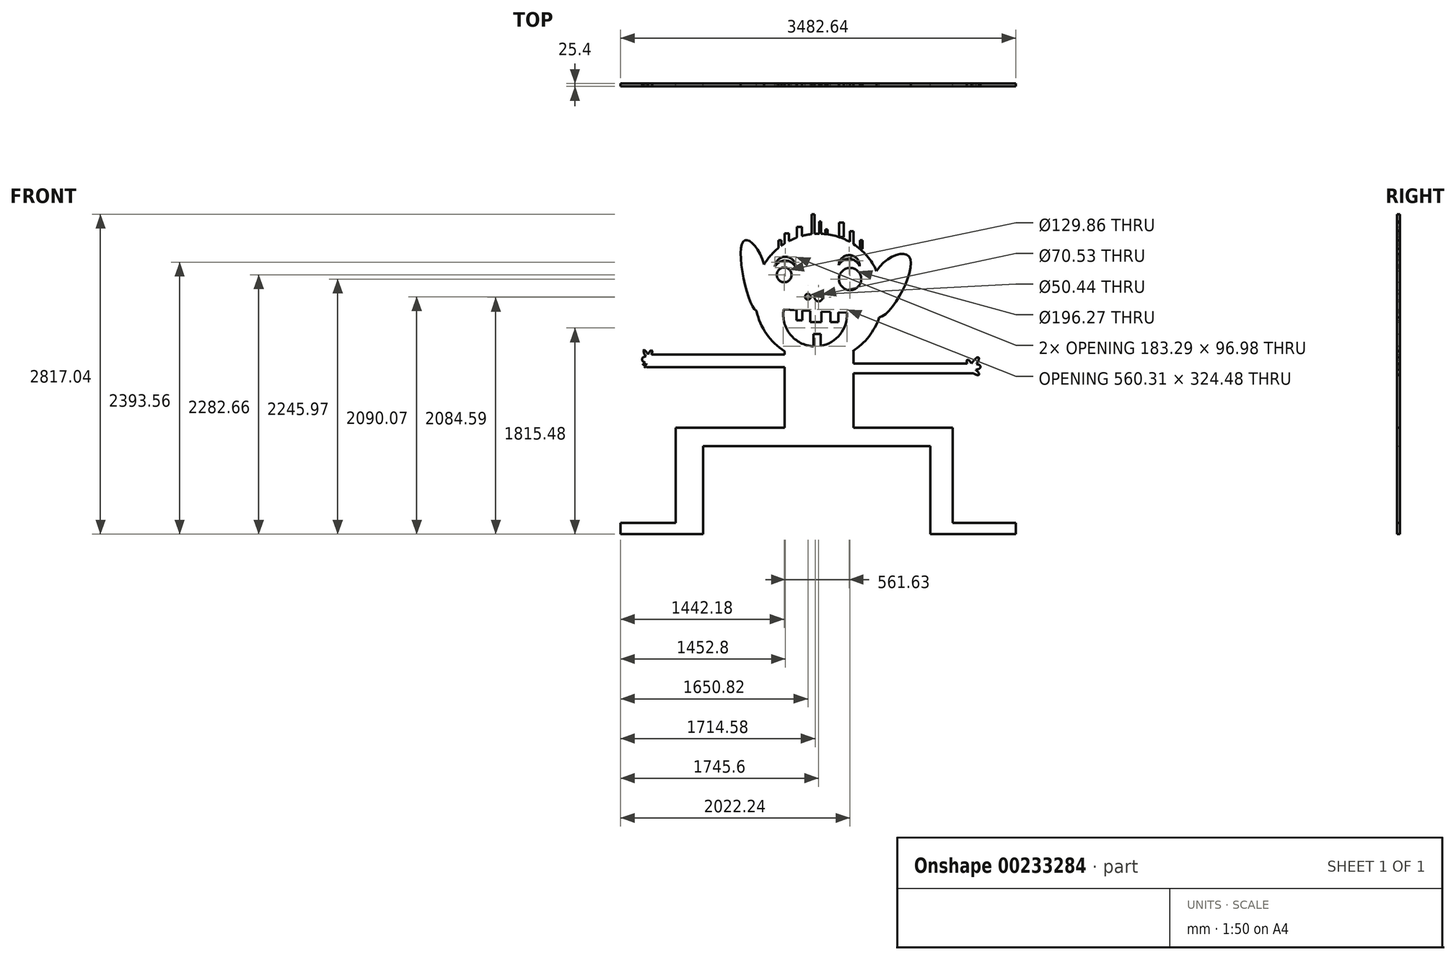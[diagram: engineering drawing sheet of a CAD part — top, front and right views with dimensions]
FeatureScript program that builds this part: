
annotation { "Feature Type Name" : "Feature", "Feature Type Description" : "" }
export const myFeature = defineFeature(function(context is Context, id is Id, definition is map)
    precondition{}
    {
        {
            var Q0;
            Q0=qCreatedBy(makeId("Front.planeOp"),FACE);
            var sketch = newSketch(context, id + "F0", { "sketchPlane" : qUnion([Q0])});
            skCircle(sketch, "E0", {"center": v(-102.15, 2084.59) * mm, "radius": 560.59 * mm});
            skLineSegment(sketch, "E1.bottom", {"start": v(-401.45, 1610.58) * mm, "end": v(205.9, 1610.58) * mm});
            skLineSegment(sketch, "E1.top", {"start": v(-401.45, 775.4) * mm, "end": v(205.9, 775.4) * mm});
            skLineSegment(sketch, "E1.left", {"start": v(-401.45, 1610.58) * mm, "end": v(-401.45, 775.4) * mm});
            skLineSegment(sketch, "E1.right", {"start": v(205.9, 1610.58) * mm, "end": v(205.9, 775.4) * mm});
            skLineSegment(sketch, "E2.bottom", {"start": v(-401.45, 775.4) * mm, "end": v(-1360, 775.4) * mm});
            skLineSegment(sketch, "E2.top", {"start": v(-401.45, 937.97) * mm, "end": v(-1360, 937.97) * mm});
            skLineSegment(sketch, "E2.left", {"start": v(-401.45, 775.4) * mm, "end": v(-401.45, 937.97) * mm});
            skLineSegment(sketch, "E2.right", {"start": v(-1360, 775.4) * mm, "end": v(-1360, 937.97) * mm});
            skLineSegment(sketch, "E3.bottom", {"start": v(-1360, 937.97) * mm, "end": v(-1120.41, 937.97) * mm});
            skLineSegment(sketch, "E3.top", {"start": v(-1360, 0) * mm, "end": v(-1120.41, 0) * mm});
            skLineSegment(sketch, "E3.left", {"start": v(-1360, 937.97) * mm, "end": v(-1360, 0) * mm});
            skLineSegment(sketch, "E3.right", {"start": v(-1120.41, 937.97) * mm, "end": v(-1120.41, 0) * mm});
            skLineSegment(sketch, "E4.bottom", {"start": v(-1120.41, 0) * mm, "end": v(-1847.75, 0) * mm});
            skLineSegment(sketch, "E4.top", {"start": v(-1120.41, 99.4) * mm, "end": v(-1847.75, 99.4) * mm});
            skLineSegment(sketch, "E4.left", {"start": v(-1120.41, 0) * mm, "end": v(-1120.41, 99.4) * mm});
            skLineSegment(sketch, "E4.right", {"start": v(-1847.75, 0) * mm, "end": v(-1847.75, 99.4) * mm});
            skLineSegment(sketch, "E5.bottom", {"start": v(205.9, 775.4) * mm, "end": v(1078.7, 775.4) * mm});
            skLineSegment(sketch, "E5.top", {"start": v(205.9, 937.97) * mm, "end": v(1078.7, 937.97) * mm});
            skLineSegment(sketch, "E5.left", {"start": v(205.9, 775.4) * mm, "end": v(205.9, 937.97) * mm});
            skLineSegment(sketch, "E5.right", {"start": v(1078.7, 775.4) * mm, "end": v(1078.7, 937.97) * mm});
            skLineSegment(sketch, "E6.bottom", {"start": v(1078.7, 937.97) * mm, "end": v(881.89, 937.97) * mm});
            skLineSegment(sketch, "E6.top", {"start": v(1078.7, 0) * mm, "end": v(881.89, 0) * mm});
            skLineSegment(sketch, "E6.left", {"start": v(1078.7, 937.97) * mm, "end": v(1078.7, 0) * mm});
            skLineSegment(sketch, "E6.right", {"start": v(881.89, 937.97) * mm, "end": v(881.89, 0) * mm});
            skLineSegment(sketch, "E7.bottom", {"start": v(881.89, 0) * mm, "end": v(1634.89, 0) * mm});
            skLineSegment(sketch, "E7.top", {"start": v(881.89, 99.4) * mm, "end": v(1634.89, 99.4) * mm});
            skLineSegment(sketch, "E7.left", {"start": v(881.89, 0) * mm, "end": v(881.89, 99.4) * mm});
            skLineSegment(sketch, "E7.right", {"start": v(1634.89, 0) * mm, "end": v(1634.89, 99.4) * mm});
            skLineSegment(sketch, "E8.bottom", {"start": v(205.9, 1417.15) * mm, "end": v(1266.94, 1417.15) * mm});
            skLineSegment(sketch, "E8.top", {"start": v(205.9, 1502.72) * mm, "end": v(1266.94, 1502.72) * mm});
            skLineSegment(sketch, "E8.left", {"start": v(205.9, 1417.15) * mm, "end": v(205.9, 1502.72) * mm});
            skLineSegment(sketch, "E8.right", {"start": v(1266.94, 1417.15) * mm, "end": v(1266.94, 1502.72) * mm});
            skLineSegment(sketch, "E9.bottom", {"start": v(-401.45, 1468.5) * mm, "end": v(-1616.71, 1468.5) * mm});
            skLineSegment(sketch, "E9.top", {"start": v(-401.45, 1579.73) * mm, "end": v(-1616.71, 1579.73) * mm});
            skLineSegment(sketch, "E9.left", {"start": v(-401.45, 1468.5) * mm, "end": v(-401.45, 1579.73) * mm});
            skLineSegment(sketch, "E9.right", {"start": v(-1616.71, 1468.5) * mm, "end": v(-1616.71, 1579.73) * mm});
            skArc(sketch, "E10", {"start": v(-410.16, 1977.72) * mm, "mid": v(-351.42, 1757.13) * mm, "end": v(-148.15, 1653.24) * mm});
            skLineSegment(sketch, "E11", {"start": v(-410.16, 1977.72) * mm, "end": v(-297.9, 1971.72) * mm});
            skCircle(sketch, "E12", {"center": v(-196.93, 2090.07) * mm, "radius": 25.22 * mm});
            skCircle(sketch, "E13", {"center": v(-102.15, 2084.59) * mm, "radius": 35.26 * mm});
            skCircle(sketch, "E14", {"center": v(-405.57, 2282.66) * mm, "radius": 64.93 * mm});
            skCircle(sketch, "E15", {"center": v(174.5, 2245.97) * mm, "radius": 98.13 * mm});
            skLineSegment(sketch, "E16.top", {"start": v(-297.9, 1883.72) * mm, "end": v(-247.37, 1883.72) * mm});
            skLineSegment(sketch, "E16.left", {"start": v(-297.9, 1971.72) * mm, "end": v(-297.9, 1883.72) * mm});
            skLineSegment(sketch, "E16.right", {"start": v(-247.37, 1971.72) * mm, "end": v(-247.37, 1883.72) * mm});
            skLineSegment(sketch, "E17.top", {"start": v(-148.15, 1762.2) * mm, "end": v(-84.59, 1762.2) * mm});
            skLineSegment(sketch, "E17.left", {"start": v(-148.15, 1653.24) * mm, "end": v(-148.15, 1762.2) * mm});
            skLineSegment(sketch, "E17.right", {"start": v(-84.59, 1653.24) * mm, "end": v(-84.59, 1762.2) * mm});
            skLineSegment(sketch, "E18.top", {"start": v(0, 1865.38) * mm, "end": v(71.32, 1865.38) * mm});
            skLineSegment(sketch, "E18.left", {"start": v(0, 1955.78) * mm, "end": v(0, 1865.38) * mm});
            skLineSegment(sketch, "E18.right", {"start": v(71.32, 1955.78) * mm, "end": v(71.32, 1865.38) * mm});
            skLineSegment(sketch, "E19.top", {"start": v(-176.11, 1867.67) * mm, "end": v(-77.71, 1867.67) * mm});
            skLineSegment(sketch, "E19.left", {"start": v(-176.11, 1965.2) * mm, "end": v(-176.11, 1867.67) * mm});
            skLineSegment(sketch, "E19.right", {"start": v(-77.71, 1965.2) * mm, "end": v(-77.71, 1867.67) * mm});
            skLineSegment(sketch, "E20.trimOffspring", {"start": v(-247.37, 1969.01) * mm, "end": v(-176.11, 1965.2) * mm});
            skLineSegment(sketch, "E21.trimOffspring", {"start": v(-77.71, 1959.94) * mm, "end": v(0, 1955.78) * mm});
            skLineSegment(sketch, "E22.trimOffspring", {"start": v(71.32, 1951.96) * mm, "end": v(146.98, 1947.92) * mm});
            skArc(sketch, "E23.trimOffspring", {"start": v(-84.59, 1657.07) * mm, "mid": v(86.3, 1758.63) * mm, "end": v(146.98, 1947.92) * mm});
            skLineSegment(sketch, "E24.bottom", {"start": v(-165.07, 2641.63) * mm, "end": v(-136.76, 2641.63) * mm});
            skLineSegment(sketch, "E24.top", {"start": v(-165.07, 2817.04) * mm, "end": v(-136.76, 2817.04) * mm});
            skLineSegment(sketch, "E24.left", {"start": v(-165.07, 2641.63) * mm, "end": v(-165.07, 2817.04) * mm});
            skLineSegment(sketch, "E24.right", {"start": v(-136.76, 2641.63) * mm, "end": v(-136.76, 2817.04) * mm});
            skLineSegment(sketch, "E25.bottom", {"start": v(-44, 2642.15) * mm, "end": v(-23.64, 2642.15) * mm});
            skLineSegment(sketch, "E25.top", {"start": v(-44, 2683.72) * mm, "end": v(-23.64, 2683.72) * mm});
            skLineSegment(sketch, "E25.left", {"start": v(-44, 2642.15) * mm, "end": v(-44, 2683.72) * mm});
            skLineSegment(sketch, "E25.right", {"start": v(-23.64, 2642.15) * mm, "end": v(-23.64, 2683.72) * mm});
            skLineSegment(sketch, "E26.bottom", {"start": v(77.54, 2615.6) * mm, "end": v(119.78, 2615.6) * mm});
            skLineSegment(sketch, "E26.top", {"start": v(77.54, 2742.3) * mm, "end": v(119.78, 2742.3) * mm});
            skLineSegment(sketch, "E26.left", {"start": v(77.54, 2615.6) * mm, "end": v(77.54, 2742.3) * mm});
            skLineSegment(sketch, "E26.right", {"start": v(119.78, 2615.6) * mm, "end": v(119.78, 2742.3) * mm});
            skLineSegment(sketch, "E27.bottom", {"start": v(172.3, 2552.42) * mm, "end": v(204.62, 2552.42) * mm});
            skLineSegment(sketch, "E27.top", {"start": v(172.3, 2667.56) * mm, "end": v(204.62, 2667.56) * mm});
            skLineSegment(sketch, "E27.left", {"start": v(172.3, 2552.42) * mm, "end": v(172.3, 2667.56) * mm});
            skLineSegment(sketch, "E27.right", {"start": v(204.62, 2552.42) * mm, "end": v(204.62, 2667.56) * mm});
            skLineSegment(sketch, "E28.bottom", {"start": v(260.43, 2512.13) * mm, "end": v(283.4, 2512.13) * mm});
            skLineSegment(sketch, "E28.top", {"start": v(260.43, 2588.78) * mm, "end": v(283.4, 2588.78) * mm});
            skLineSegment(sketch, "E28.left", {"start": v(260.43, 2512.13) * mm, "end": v(260.43, 2588.78) * mm});
            skLineSegment(sketch, "E28.right", {"start": v(283.4, 2512.13) * mm, "end": v(283.4, 2588.78) * mm});
            skLineSegment(sketch, "E29.bottom", {"start": v(-401.38, 2647.36) * mm, "end": v(-365.02, 2647.36) * mm});
            skLineSegment(sketch, "E29.top", {"start": v(-401.38, 2516.07) * mm, "end": v(-365.02, 2516.07) * mm});
            skLineSegment(sketch, "E29.left", {"start": v(-401.38, 2647.36) * mm, "end": v(-401.38, 2516.07) * mm});
            skLineSegment(sketch, "E29.right", {"start": v(-365.02, 2647.36) * mm, "end": v(-365.02, 2516.07) * mm});
            skLineSegment(sketch, "E30.bottom", {"start": v(-292.3, 2705.94) * mm, "end": v(-249.88, 2705.94) * mm});
            skLineSegment(sketch, "E30.top", {"start": v(-292.3, 2532.23) * mm, "end": v(-249.88, 2532.23) * mm});
            skLineSegment(sketch, "E30.left", {"start": v(-292.3, 2705.94) * mm, "end": v(-292.3, 2532.23) * mm});
            skLineSegment(sketch, "E30.right", {"start": v(-249.88, 2705.94) * mm, "end": v(-249.88, 2532.23) * mm});
            skLineSegment(sketch, "E31.bottom", {"start": v(-455.92, 2586.76) * mm, "end": v(-429.66, 2586.76) * mm});
            skLineSegment(sketch, "E31.top", {"start": v(-455.92, 2489.8) * mm, "end": v(-429.66, 2489.8) * mm});
            skLineSegment(sketch, "E31.left", {"start": v(-455.92, 2586.76) * mm, "end": v(-455.92, 2489.8) * mm});
            skLineSegment(sketch, "E31.right", {"start": v(-429.66, 2586.76) * mm, "end": v(-429.66, 2489.8) * mm});
            skLineSegment(sketch, "E32.bottom", {"start": v(-98.38, 2752.4) * mm, "end": v(-82.22, 2752.4) * mm});
            skLineSegment(sketch, "E32.top", {"start": v(-98.38, 2606.96) * mm, "end": v(-82.22, 2606.96) * mm});
            skLineSegment(sketch, "E32.left", {"start": v(-98.38, 2752.4) * mm, "end": v(-98.38, 2606.96) * mm});
            skLineSegment(sketch, "E32.right", {"start": v(-82.22, 2752.4) * mm, "end": v(-82.22, 2606.96) * mm});
            skFitSpline(sketch, "E33", {"points": [v(408.41, 2316.07) * mm, v(702.68, 2426.97) * mm, v(430.43, 1909.6) * mm, v(408.41, 2316.07) * mm]});
            skFitSpline(sketch, "E34", {"points": [v(-581.43, 2375.35) * mm, v(-769.97, 2571.6) * mm, v(-649.73, 1964.52) * mm, v(-581.43, 2375.35) * mm]});
            skEllipticalArc(sketch, "E35", {});
            skEllipticalArc(sketch, "E36", {});
            skEllipticalArc(sketch, "E37", {});
            skEllipticalArc(sketch, "E38", {});
            skEllipticalArc(sketch, "E39", {});
            skPoint(sketch, "E39.centerSnap0", {"position": v(-1616.71, 1524.11) * mm});
            skEllipticalArc(sketch, "E40", {});
            skEllipticalArc(sketch, "E41.trimOffspring", {});
            skEllipticalArc(sketch, "E42.trimOffspring", {});
            skEllipticalArc(sketch, "E43.trimOffspring", {});
            skArc(sketch, "E44", {"start": v(-303.31, 2344.94) * mm, "mid": v(-390.01, 2442.04) * mm, "end": v(-486.6, 2354.76) * mm});
            skArc(sketch, "E45", {"start": v(-303.25, 2344.94) * mm, "mid": v(-391.79, 2408.44) * mm, "end": v(-486.6, 2354.76) * mm});
            skArc(sketch, "E46", {"start": v(258.32, 2359.27) * mm, "mid": v(171.62, 2456.37) * mm, "end": v(75.04, 2369.1) * mm});
            skArc(sketch, "E47", {"start": v(258.38, 2359.27) * mm, "mid": v(169.85, 2422.77) * mm, "end": v(75.04, 2369.1) * mm});
            const initialGuessF0  = {"E35": [1.266944409318715, 1.4347364902496338, 0.7979302437208883, -0.602749803944824, 0.053229956455536125, 0.017958525905336444, 4.8163796118201265, 1.510735944085237], "E36": [1.2238599061965942, 1.5027223120034157, -0.509668370672036, 0.8603709385704007, 0.03624472653408108, 0.01585344580389217, 4.400556035408517, 1.3172639835627318], "E37": [-1.6167120062929308, 1.5797338336314164, -0.5395379565913592, 0.8419612778490593, 0.04824150704059213, 0.012581095540696769, 4.546799609546494, 1.957301117754438], "E38": [-1.6167120062929308, 1.5368421077728271, -0.9947786774732179, 0.10205578300437237, 0.040463449280004955, 0.027040895779368267, 4.780841627586596, 1.6392489739968026], "E39": [-1.6167120062929308, 1.5097229429932708, -0.8756909755827507, -0.4828719450153742, 0.03601074224345466, 0.008199329894835888, 4.587489447429465, 1.4458967938396718], "E40": [-1.6167120062929308, 1.488663673400879, -0.7135934271198743, -0.7005600764897417, 0.025543653831947215, 0.006988045743256301, 4.450004829819142, 1.3084121762293492], "E41.trimOffspring": [-1.5895144939422607, 1.5797338336314164, 0.4272878961909681, 0.9041156196906989, 0.041880109972360795, 0.013994264362789357, 4.869016124479393, 1.7274234708896], "E42.trimOffspring": [1.266944409318715, 1.5027223120034157, 0.5916707379241914, 0.806179718105239, 0.06521314270312492, 0.019172208784876153, 4.823235003051081, 1.8182121997483216], "E43.trimOffspring": [1.266944409318715, 1.472642423368864, 1, 0, 0.056085347227305515, 0.026283927829567316, 4.952807612019513, 1.2132304432235903]};
            skSetInitialGuess(sketch, initialGuessF0);
            skSolve(sketch);
        }
        {
            var Q0;
            Q0 = qSketchRegion(id + "F0", true);
            extrude(context, id + "F1", {"entities" : qUnion([Q0]), "depth" : 25.4 * mm});
        }
    });
